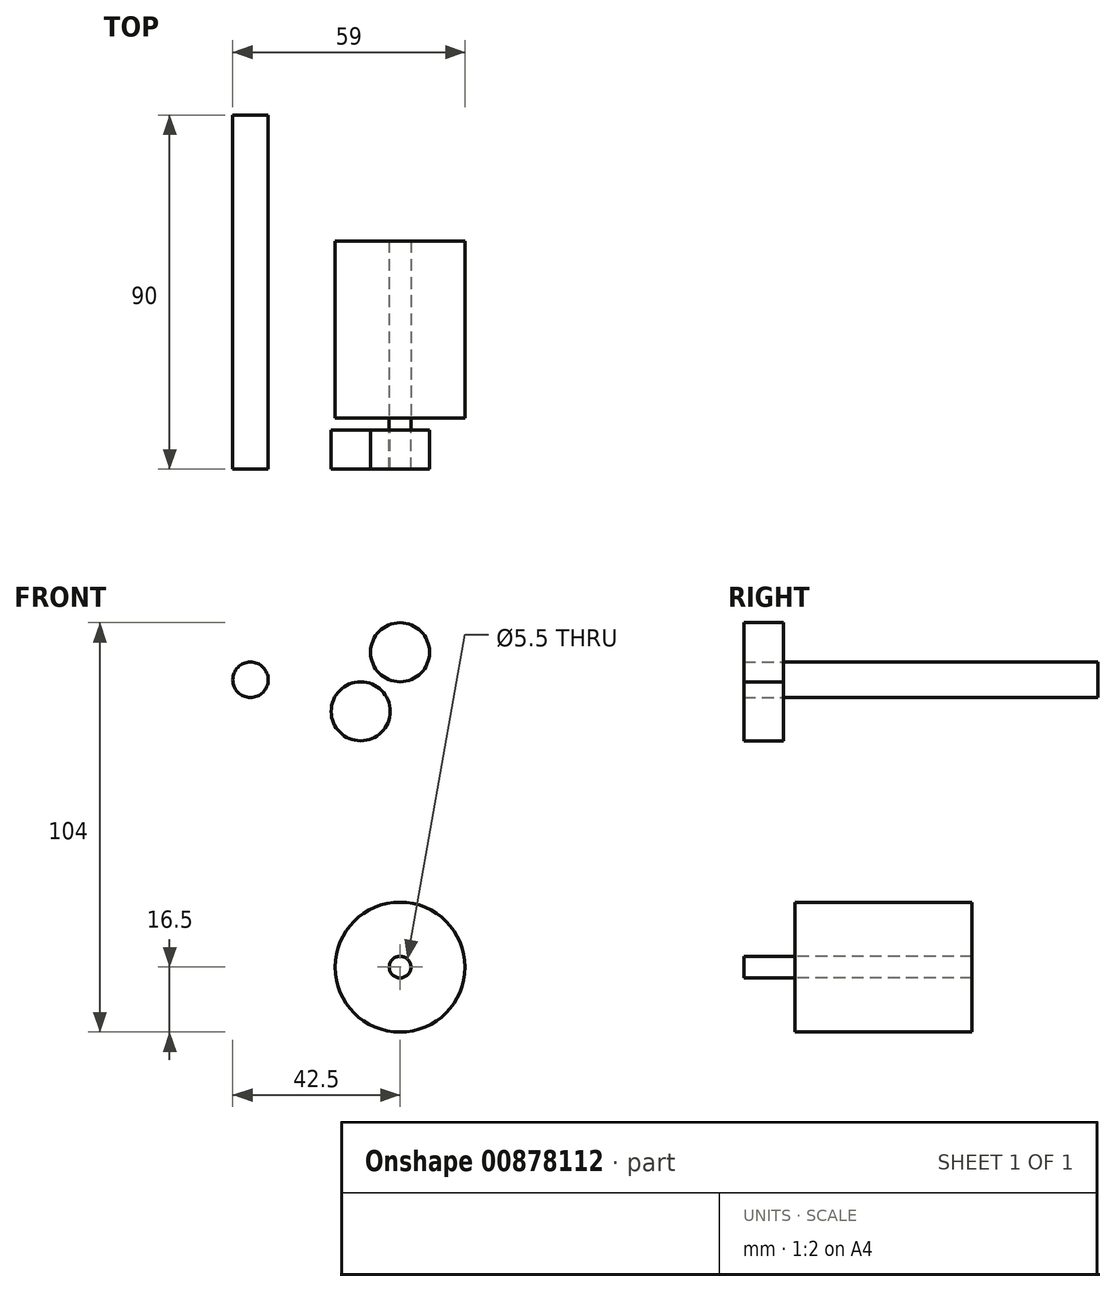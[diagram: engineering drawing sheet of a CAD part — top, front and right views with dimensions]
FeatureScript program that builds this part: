
annotation { "Feature Type Name" : "Feature", "Feature Type Description" : "" }
export const myFeature = defineFeature(function(context is Context, id is Id, definition is map)
    precondition{}
    {
        {
            var Q0;
            Q0=qCreatedBy(makeId("Front.planeOp"),FACE);
            var sketch = newSketch(context, id + "F0", { "sketchPlane" : qUnion([Q0])});
            skCircle(sketch, "E0", {"center": v(0, 0) * mm, "radius": 2.75 * mm});
            skLineSegment(sketch, "E1", {"start": v(0, 0) * mm, "end": v(0, 80) * mm, "construction": true});
            skLineSegment(sketch, "E2", {"start": v(0, 0) * mm, "end": v(0, 65) * mm, "construction": true});
            skLineSegment(sketch, "E3", {"start": v(0, 65) * mm, "end": v(-10, 65) * mm, "construction": true});
            skCircle(sketch, "E4", {"center": v(0, 80) * mm, "radius": 7.5 * mm});
            skCircle(sketch, "E5", {"center": v(-10, 65) * mm, "radius": 7.5 * mm});
            skLineSegment(sketch, "E6", {"start": v(0, 0) * mm, "end": v(0, 73) * mm, "construction": true});
            skLineSegment(sketch, "E7", {"start": v(0, 73) * mm, "end": v(-38, 73) * mm, "construction": true});
            skCircle(sketch, "E8", {"center": v(-38, 73) * mm, "radius": 4.5 * mm});
            skArc(sketch, "E9", {"start": v(-39.97, 78.13) * mm, "mid": v(-43.35, 71.74) * mm, "end": v(-37.48, 67.52) * mm});
            skArc(sketch, "E10", {"start": v(8.6, 77.36) * mm, "mid": v(6.63, 86.08) * mm, "end": v(-1.89, 88.8) * mm});
            skArc(sketch, "E11", {"start": v(-1.07, 63.9) * mm, "mid": v(-3.85, 71.57) * mm, "end": v(-11.69, 73.84) * mm});
            skArc(sketch, "E12", {"start": v(-3.39, 0.87) * mm, "mid": v(-0.57, -3.45) * mm, "end": v(3.5, -0.26) * mm});
            skLineSegment(sketch, "E13", {"start": v(-37.48, 67.52) * mm, "end": v(-11.69, 73.84) * mm});
            skLineSegment(sketch, "E14", {"start": v(-39.97, 78.13) * mm, "end": v(-1.89, 88.8) * mm});
            skLineSegment(sketch, "E15", {"start": v(8.6, 77.36) * mm, "end": v(3.5, -0.26) * mm});
            skLineSegment(sketch, "E16", {"start": v(-1.07, 63.9) * mm, "end": v(-3.39, 0.87) * mm});
            skLineSegment(sketch, "E17", {"start": v(-11.69, 73.84) * mm, "end": v(-10, 65) * mm, "construction": true});
            skLineSegment(sketch, "E18", {"start": v(-38, 73) * mm, "end": v(-37.48, 67.52) * mm, "construction": true});
            skLineSegment(sketch, "E19", {"start": v(-1.89, 88.8) * mm, "end": v(0, 80) * mm, "construction": true});
            skLineSegment(sketch, "E20", {"start": v(0, 0) * mm, "end": v(-2.7, -2.22) * mm, "construction": true});
            skSolve(sketch);
        }
        {
            var Q0;
            Q0=makeQuery(id+"F0.imprint","IMPRINT",FACE,{"disambiguationData":[TD([[makeQuery(id+"F0.imprint","IMPRINT",EDGE,{"derivedFrom":sQuery(id+"F0.wireOp",EDGE,"E4")}),1.0]])]});
            var Q1;
            Q1=makeQuery(id+"F0.imprint","IMPRINT",FACE,{"disambiguationData":[TD([[makeQuery(id+"F0.imprint","IMPRINT",EDGE,{"derivedFrom":sQuery(id+"F0.wireOp",EDGE,"E8")}),1.0]])]});
            var Q2;
            Q2=makeQuery(id+"F0.imprint","IMPRINT",FACE,{"disambiguationData":[TD([[makeQuery(id+"F0.imprint","IMPRINT",EDGE,{"derivedFrom":sQuery(id+"F0.wireOp",EDGE,"E5")}),1.0]])]});
            var Q3;
            Q3=makeQuery(id+"F0.imprint","IMPRINT",FACE,{"disambiguationData":[TD([[makeQuery(id+"F0.imprint","IMPRINT",EDGE,{"derivedFrom":sQuery(id+"F0.wireOp",EDGE,"E0")}),1.0]])]});
            extrude(context, id + "F1", {"entities" : qUnion([Q0, Q1, Q2, Q3]), "depth" : 10 * mm, "offsetDistance" : 25 * mm});
        }
        {
            var Q0;
            Q0=sQuery(id+"F0.wireOp",EDGE,"E14");
            var Q1;
            Q1=sQuery(id+"F0.wireOp",EDGE,"E9");
            var Q2;
            Q2=sQuery(id+"F0.wireOp",EDGE,"E13");
            var Q3;
            Q3=sQuery(id+"F0.wireOp",EDGE,"E11");
            var Q4;
            Q4=sQuery(id+"F0.wireOp",EDGE,"E15");
            var Q5;
            Q5=sQuery(id+"F0.wireOp",EDGE,"E10");
            var Q6;
            Q6=sQuery(id+"F0.wireOp",EDGE,"E12");
            var Q7;
            Q7=sQuery(id+"F0.wireOp",EDGE,"E16");
            extrude(context, id + "F2", {"bodyType" : ToolBodyType.SURFACE, "surfaceEntities" : qUnion([Q0, Q1, Q2, Q3, Q4, Q5, Q6, Q7]), "depth" : 8 * mm, "offsetDistance" : 25 * mm});
        }
        {
            var Q0;
            Q0=makeQuery(id+"F1.opExtrude","CAP_FACE",FACE,{"disambiguationData":[OSD([sQuery(id+"F0.wireOp",EDGE,"E8")])],"isStart":true});
            var sketch = newSketch(context, id + "F3", { "sketchPlane" : qUnion([Q0])});
            skCircle(sketch, "E21", {"center": v(38, 73) * mm, "radius": 4.5 * mm});
            skSolve(sketch);
        }
        {
            var Q0;
            Q0=makeQuery(id+"F3.imprint","IMPRINT",FACE,{"disambiguationData":[TD([[makeQuery(id+"F3.imprint","IMPRINT",EDGE,{"derivedFrom":sQuery(id+"F3.wireOp",EDGE,"E21")}),-1.0]])]});
            extrude(context, id + "F4", {"entities" : qUnion([Q0]), "operationType" : NewBodyOperationType.ADD, "depth" : 80 * mm, "offsetDistance" : 25 * mm});
        }
        {
            var Q0;
            Q0=makeQuery(id+"F1.opExtrude","CAP_FACE",FACE,{"disambiguationData":[OSD([sQuery(id+"F0.wireOp",EDGE,"E0")])],"isStart":true});
            var sketch = newSketch(context, id + "F5", { "sketchPlane" : qUnion([Q0])});
            skCircle(sketch, "E22", {"center": v(0, 0) * mm, "radius": 2.75 * mm});
            skSolve(sketch);
        }
        {
            var Q0;
            Q0=makeQuery(id+"F5.imprint","IMPRINT",FACE,{"disambiguationData":[TD([[makeQuery(id+"F5.imprint","IMPRINT",EDGE,{"derivedFrom":sQuery(id+"F5.wireOp",EDGE,"E22")}),-1.0]])]});
            extrude(context, id + "F6", {"entities" : qUnion([Q0]), "operationType" : NewBodyOperationType.ADD, "depth" : 3 * mm, "offsetDistance" : 25 * mm});
        }
        {
            var Q0;
            Q0=makeQuery(id+"F6.opExtrude","CAP_FACE",FACE,{"disambiguationData":[OSD([sQuery(id+"F5.wireOp",EDGE,"E22")])],"isStart":false});
            var sketch = newSketch(context, id + "F7", { "sketchPlane" : qUnion([Q0])});
            skCircle(sketch, "E23", {"center": v(0, 0) * mm, "radius": 16.5 * mm});
            skSolve(sketch);
        }
        {
            var Q0;
            Q0=makeQuery(id+"F7.imprint","IMPRINT",FACE,{"disambiguationData":[TD([[makeQuery(id+"F7.imprint","IMPRINT",EDGE,{"derivedFrom":sQuery(id+"F7.wireOp",EDGE,"E23")}),1.0]])]});
            extrude(context, id + "F8", {"entities" : qUnion([Q0]), "depth" : 45 * mm, "offsetDistance" : 25 * mm});
        }
    });
